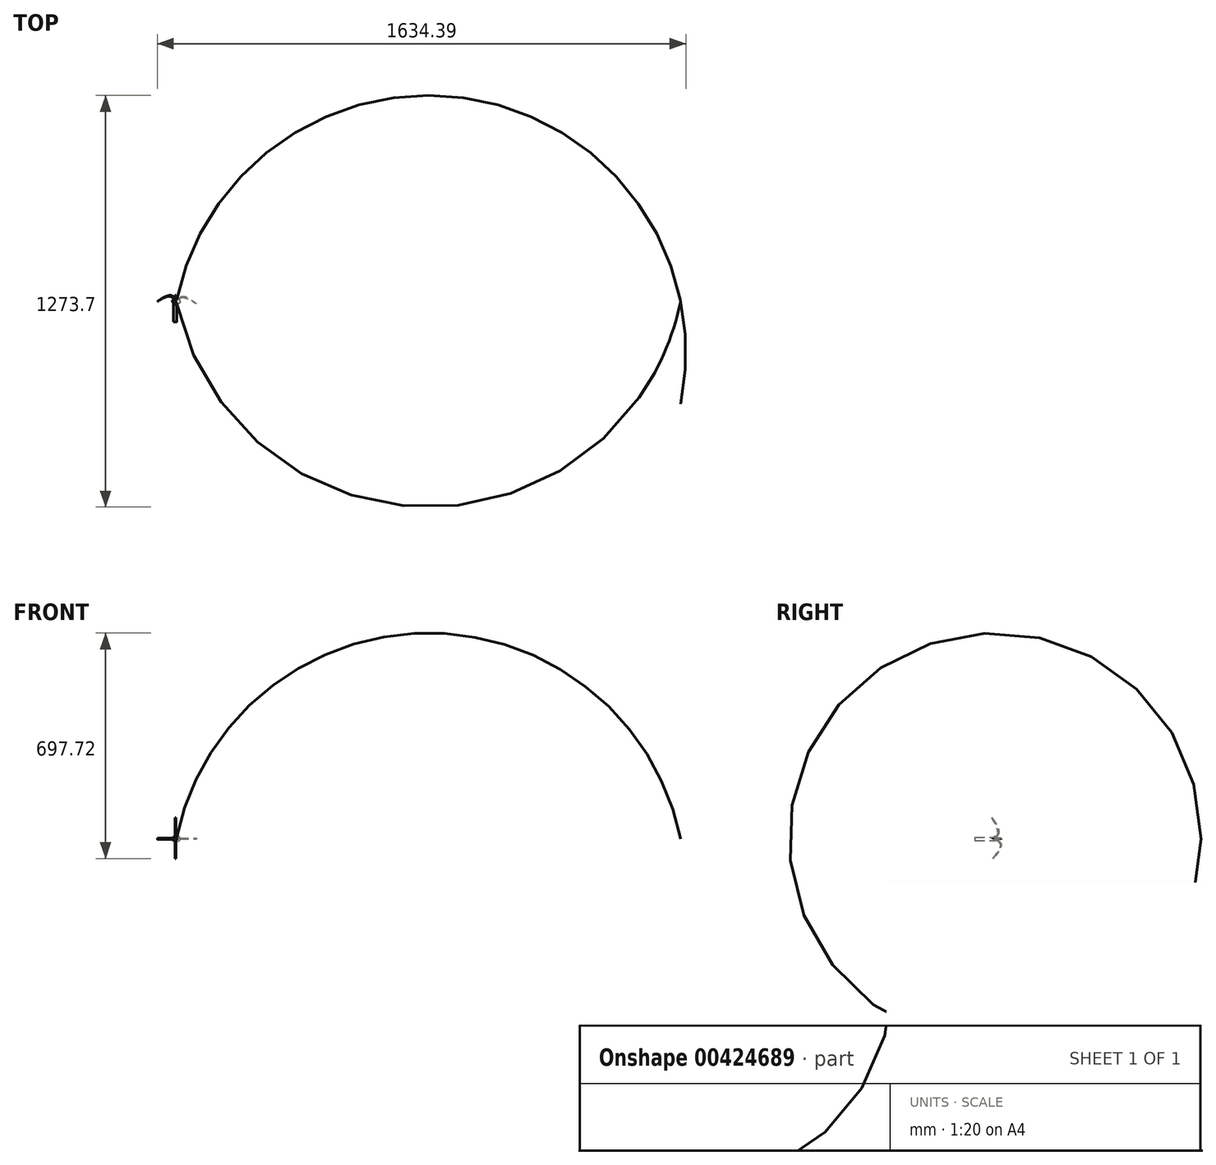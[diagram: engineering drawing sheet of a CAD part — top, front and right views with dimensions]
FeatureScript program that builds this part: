
annotation { "Feature Type Name" : "Feature", "Feature Type Description" : "" }
export const myFeature = defineFeature(function(context is Context, id is Id, definition is map)
    precondition{}
    {
        {
            var Q0;
            Q0=qCreatedBy(makeId("Top.planeOp"),FACE);
            var sketch = newSketch(context, id + "F0", { "sketchPlane" : qUnion([Q0])});
            skCircle(sketch, "E0", {"center": v(-2.57, -0.22) * mm, "radius": 6 * mm});
            skPoint(sketch, "E0.first.point", {"position": v(-6.03, 4.68) * mm});
            skPoint(sketch, "E0.second.point", {"position": v(0.94, -5.1) * mm});
            skPoint(sketch, "E0.third.point", {"position": v(3.43, 0) * mm});
            skCircle(sketch, "E1", {"center": v(8.94, 0) * mm, "radius": 6.9 * mm});
            skLineSegment(sketch, "E2", {"start": v(-13, 0) * mm, "end": v(20.69, 0) * mm});
            skFitSpline(sketch, "E3", {"points": [v(0, 0) * mm, v(-3.9, -45.1) * mm, v(0, -73.94) * mm, v(0, -74.86) * mm], "startDerivative": vector(-14, -85.64) * mm, "endDerivative": vector(-1.1, -8.07) * mm});
            skFitSpline(sketch, "E4", {"points": [v(3.43, 0) * mm, v(0, -32.74) * mm, v(5.04, -74.86) * mm, v(5.72, -74.63) * mm], "startDerivative": vector(-12.55, -61.75) * mm, "endDerivative": vector(10.3, 9.48) * mm});
            skLineSegment(sketch, "E5", {"start": v(0, -74.86) * mm, "end": v(5.72, -74.63) * mm});
            skLineSegment(sketch, "E6", {"start": v(3.43, 0) * mm, "end": v(0, 0) * mm});
            skSolve(sketch);
        }
        {
            var Q0;
            {var subQ0=sQuery(id+"F0.wireOp",EDGE,"E1");var subQ1=sQuery(id+"F0.wireOp",EDGE,"E0");var subQ2=makeQuery(id+"F0.imprint","INTERSECT",VERTEX,{"disambiguationData":[OD(0.0)],"derivedFrom":[subQ1,subQ0]});Q0=makeQuery(id+"F0.imprint","IMPRINT",FACE,{"disambiguationData":[TD([[makeQuery(id+"F0.imprint","IMPRINT",EDGE,{"disambiguationData":[TD([[subQ2,1.0]])],"derivedFrom":subQ1}),-1.0]])]});}
            var Q1;
            {var subQ0=sQuery(id+"F0.wireOp",EDGE,"E2");var subQ1=sQuery(id+"F0.wireOp",EDGE,"E0");var subQ2=makeQuery(id+"F0.imprint","INTERSECT",VERTEX,{"disambiguationData":[OD(0.0)],"derivedFrom":[subQ1,subQ0]});Q1=makeQuery(id+"F0.imprint","IMPRINT",FACE,{"disambiguationData":[TD([[makeQuery(id+"F0.imprint","IMPRINT",EDGE,{"disambiguationData":[TD([[subQ2,1.0]])],"derivedFrom":subQ1}),1.0]])]});}
            var Q2;
            {var subQ0=sQuery(id+"F0.wireOp",EDGE,"E1");var subQ1=sQuery(id+"F0.wireOp",EDGE,"E0");var subQ2=makeQuery(id+"F0.imprint","INTERSECT",VERTEX,{"disambiguationData":[OD(1.0)],"derivedFrom":[subQ1,subQ0]});Q2=makeQuery(id+"F0.imprint","IMPRINT",FACE,{"disambiguationData":[TD([[makeQuery(id+"F0.imprint","IMPRINT",EDGE,{"disambiguationData":[TD([[subQ2,-1.0]])],"derivedFrom":subQ1}),1.0]])]});}
            var Q3;
            Q3=sQuery(id+"F0.wireOp",EDGE,"E2");
            revolve(context, id + "F1", {"entities" : qUnion([Q0, Q1, Q2]), "axis" : qUnion([Q3]), "revolveType" : RevolveType.FULL});
        }
        {
            var Q0;
            Q0=qCreatedBy(makeId("Top.planeOp"),FACE);
            var sketch = newSketch(context, id + "F2", { "sketchPlane" : qUnion([Q0])});
            skFitSpline(sketch, "E7", {"points": [v(0, 0) * mm, v(-16.11, 18.28) * mm, v(-54.14, 0) * mm, v(-54.28, 0) * mm], "startDerivative": vector(-23.27, 66.8) * mm, "endDerivative": vector(-2.1, 1.72) * mm});
            skFitSpline(sketch, "E8", {"points": [v(0, 0) * mm, v(-15.7, 15.23) * mm, v(-54.14, 0) * mm], "startDerivative": vector(-31.15, 49.33) * mm, "endDerivative": vector(-74.84, -44.4) * mm});
            skFitSpline(sketch, "E9", {"points": [v(0, 0) * mm, v(-13.35, 16.2) * mm, v(-54.14, 0) * mm], "startDerivative": vector(-25.21, 53.33) * mm, "endDerivative": vector(-79.76, -47.22) * mm});
            skSolve(sketch);
        }
        {
            var Q0;
            Q0 = qSketchRegion(id + "F2", true);
            extrude(context, id + "F3", {"entities" : qUnion([Q0]), "depth" : 2 * mm, "hasDraft" : true, "draftAngle" : 3 * degree, "hasSecondDirection" : true, "secondDirectionOppositeDirection" : true, "secondDirectionDepth" : 2 * mm});
        }
        {
            var Q0;
            Q0=qCreatedBy(makeId("Top.planeOp"),FACE);
            var sketch = newSketch(context, id + "F4", { "sketchPlane" : qUnion([Q0])});
            skFitSpline(sketch, "E10", {"points": [v(6.5, 0) * mm, v(22.34, 15.38) * mm, v(66.15, -7.9) * mm], "startDerivative": vector(32.9, 53.87) * mm, "endDerivative": vector(83.07, -61.96) * mm});
            skFitSpline(sketch, "E11", {"points": [v(6.5, 0) * mm, v(21.55, 11.66) * mm, v(66.15, -7.9) * mm], "startDerivative": vector(32.73, 42.25) * mm, "endDerivative": vector(82.74, -50.9) * mm});
            skSolve(sketch);
        }
        {
            var Q0;
            Q0 = qSketchRegion(id + "F4", true);
            extrude(context, id + "F5", {"entities" : qUnion([Q0]), "operationType" : NewBodyOperationType.ADD, "depth" : 2 * mm});
        }
        {
            var Q0;
            Q0=qCreatedBy(makeId("Right.planeOp"),FACE);
            var sketch = newSketch(context, id + "F6", { "sketchPlane" : qUnion([Q0])});
            skFitSpline(sketch, "E12", {"points": [v(0, -2) * mm, v(18.11, -21.36) * mm, v(-8.1, -60.87) * mm, v(-8.3, -60.47) * mm], "startDerivative": vector(72.54, -32.54) * mm, "endDerivative": vector(-0.17, 11.92) * mm});
            skFitSpline(sketch, "E13", {"points": [v(0, -2) * mm, v(15.77, -18.23) * mm, v(-8.1, -60.87) * mm], "startDerivative": vector(54.94, -33.7) * mm, "endDerivative": vector(-63.61, -81.05) * mm});
            skSolve(sketch);
        }
        {
            var Q0;
            Q0 = qSketchRegion(id + "F6", true);
            extrude(context, id + "F7", {"entities" : qUnion([Q0]), "operationType" : NewBodyOperationType.ADD, "depth" : 2 * mm});
        }
        {
            var Q0;
            Q0=qCreatedBy(makeId("Right.planeOp"),FACE);
            var sketch = newSketch(context, id + "F8", { "sketchPlane" : qUnion([Q0])});
            skFitSpline(sketch, "E14", {"points": [v(0, 2.97) * mm, v(11.85, 25.47) * mm, v(-10.44, 65.56) * mm, v(-10.64, 65.56) * mm], "startDerivative": vector(49.91, 41.87) * mm, "endDerivative": vector(-3.48, -2.75) * mm});
            skFitSpline(sketch, "E15", {"points": [v(0, 2.97) * mm, v(8.33, 18.62) * mm, v(-10.44, 65.56) * mm], "startDerivative": vector(32.14, 36) * mm, "endDerivative": vector(-46.32, 85) * mm});
            skSolve(sketch);
        }
        {
            var Q0;
            Q0 = qSketchRegion(id + "F8", true);
            extrude(context, id + "F9", {"entities" : qUnion([Q0]), "operationType" : NewBodyOperationType.ADD, "depth" : 2 * mm});
        }
        {
            var Q0;
            Q0=qCreatedBy(makeId("Right.planeOp"),FACE);
            var sketch = newSketch(context, id + "F10", { "sketchPlane" : qUnion([Q0])});
            skLineSegment(sketch, "E16", {"start": v(0, 0) * mm, "end": v(-63.33, 0) * mm});
            skLineSegment(sketch, "E17", {"start": v(-63.33, 0) * mm, "end": v(-63.33, 5.08) * mm});
            skLineSegment(sketch, "E18", {"start": v(-63.33, 5.08) * mm, "end": v(0, 5.08) * mm});
            skLineSegment(sketch, "E19", {"start": v(0, 5.08) * mm, "end": v(0, 0) * mm});
            skSolve(sketch);
        }
        {
            var Q0;
            Q0=makeQuery(id+"F10.imprint","IMPRINT",FACE,{"disambiguationData":[TD([[makeQuery(id+"F10.imprint","IMPRINT",EDGE,{"derivedFrom":sQuery(id+"F10.wireOp",EDGE,"E16")}),-1.0]])]});
            var Q1;
            Q1=sQuery(id+"F10.wireOp",EDGE,"E16");
            revolve(context, id + "F11", {"entities" : qUnion([Q0]), "axis" : qUnion([Q1]), "revolveType" : RevolveType.FULL});
        }
    });
